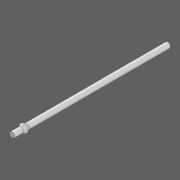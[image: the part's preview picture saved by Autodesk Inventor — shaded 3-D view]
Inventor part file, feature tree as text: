
AUTODESK INVENTOR PART (.ipt)
format: ipt  version: 2020 (Build 240168000, 168)  size: 91,648 bytes
history: native  units: in
note: dims shown in document units (in); Inventor stores cm internally (conversion verified against a paired STEP export)
features: revolve x1, fillet x1, sketch x1
ambient origin geometry x8: Origin, YZ Plane, XZ Plane, XY Plane, X Axis, Y Axis, Z Axis, Center Point
bodies: Solid1 (feature_tree)
feature tree (3):
  revolve  "Revolution1"  [1 undecoded]
  fillet  "Fillet1"  Radius=0.1969in
  sketch  "Sketch1"  dims[d0=90.0deg d5=7.0866in d8=0.1969in d12=0.2362in d13=0.2756in d14=0.3937in d15=0.2756in]
note: 1 required parameter value undecoded (feature->parameter linkage not recoverable at this tier; creation-order binding heuristic only, values carry confidence <= 0.55)
